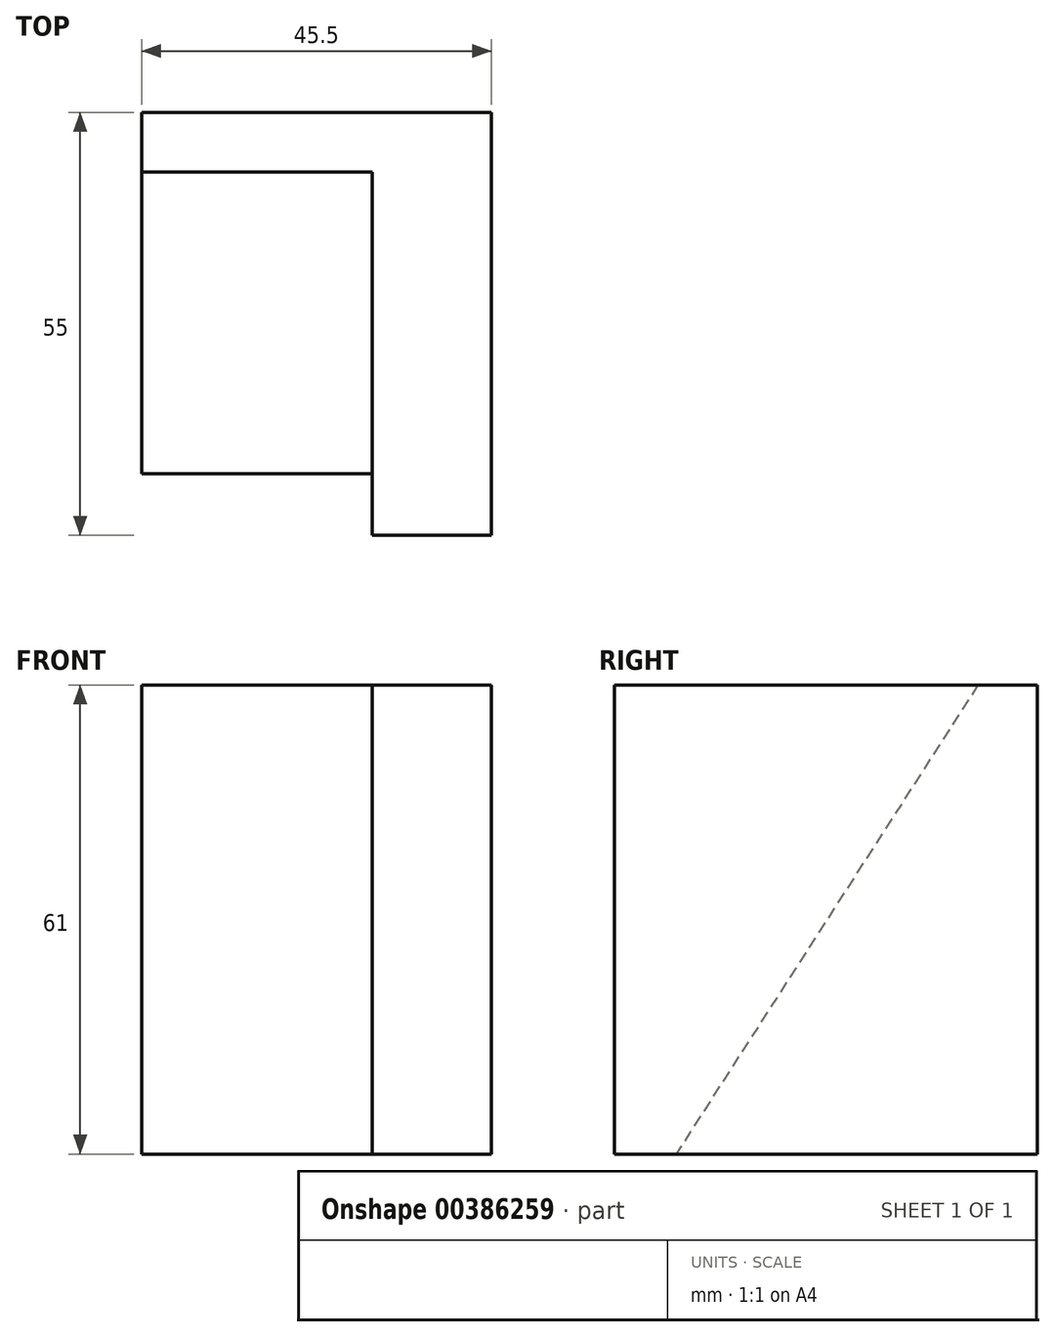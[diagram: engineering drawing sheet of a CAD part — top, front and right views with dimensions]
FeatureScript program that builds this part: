
annotation { "Feature Type Name" : "Feature", "Feature Type Description" : "" }
export const myFeature = defineFeature(function(context is Context, id is Id, definition is map)
    precondition{}
    {
        {
            var Q0;
            Q0=qCreatedBy(makeId("Front.planeOp"),FACE);
            var sketch = newSketch(context, id + "F0", { "sketchPlane" : qUnion([Q0])});
            skLineSegment(sketch, "E0", {"start": v(-30.5, 0) * mm, "end": v(-99.5, 0) * mm});
            skLineSegment(sketch, "E1", {"start": v(30.5, 0) * mm, "end": v(99.5, 0) * mm});
            skLineSegment(sketch, "E2", {"start": v(-99.5, 0) * mm, "end": v(-99.5, 15) * mm});
            skLineSegment(sketch, "E3", {"start": v(-99.5, 15) * mm, "end": v(-30.5, 15) * mm});
            skLineSegment(sketch, "E4", {"start": v(-30.5, 15) * mm, "end": v(-30.5, 0) * mm});
            skLineSegment(sketch, "E5", {"start": v(99.5, 0) * mm, "end": v(99.5, 15) * mm});
            skLineSegment(sketch, "E6", {"start": v(99.5, 15) * mm, "end": v(30.5, 15) * mm});
            skLineSegment(sketch, "E7", {"start": v(30.5, 15) * mm, "end": v(30.5, 0) * mm});
            skLineSegment(sketch, "E8", {"start": v(-30.5, 15) * mm, "end": v(-30.5, 61) * mm});
            skLineSegment(sketch, "E9", {"start": v(30.5, 61) * mm, "end": v(30.5, 15) * mm});
            skLineSegment(sketch, "E10", {"start": v(-30.5, 0) * mm, "end": v(-15, 0) * mm});
            skLineSegment(sketch, "E11", {"start": v(-15, 0) * mm, "end": v(15, 0) * mm});
            skLineSegment(sketch, "E12", {"start": v(15, 0) * mm, "end": v(30.5, 0) * mm});
            skLineSegment(sketch, "E13", {"start": v(-15, 0) * mm, "end": v(-15, 61) * mm});
            skLineSegment(sketch, "E14", {"start": v(30.5, 61) * mm, "end": v(-30.5, 61) * mm});
            skLineSegment(sketch, "E15", {"start": v(15, 0) * mm, "end": v(15, 61) * mm});
            skSolve(sketch);
        }
        {
            var Q0;
            Q0=makeQuery(id+"F0.imprint","IMPRINT",FACE,{"disambiguationData":[TD([[makeQuery(id+"F0.imprint","IMPRINT",EDGE,{"derivedFrom":sQuery(id+"F0.wireOp",EDGE,"E7")}),-1.0]])]});
            extrude(context, id + "F1", {"entities" : qUnion([Q0]), "depth" : 55 * mm});
        }
        {
            var Q0;
            Q0=makeQuery(id+"F1.opExtrude","SWEPT_FACE",FACE,{"disambiguationData":[OSD([sQuery(id+"F0.wireOp",EDGE,"E15")])]});
            var sketch = newSketch(context, id + "F2", { "sketchPlane" : qUnion([Q0])});
            skLineSegment(sketch, "E16", {"start": v(0, 61) * mm, "end": v(7.75, 61) * mm});
            skLineSegment(sketch, "E17", {"start": v(7.75, 61) * mm, "end": v(47, 0) * mm});
            skLineSegment(sketch, "E18", {"start": v(47, 0) * mm, "end": v(0, 0) * mm});
            skLineSegment(sketch, "E19", {"start": v(0, 0) * mm, "end": v(0, 61) * mm});
            skSolve(sketch);
        }
        {
            var Q0;
            Q0=makeQuery(id+"F2.imprint","IMPRINT",FACE,{"disambiguationData":[TD([[makeQuery(id+"F2.imprint","IMPRINT",EDGE,{"derivedFrom":sQuery(id+"F2.wireOp",EDGE,"E16")}),1.0]])]});
            extrude(context, id + "F3", {"entities" : qUnion([Q0]), "operationType" : NewBodyOperationType.ADD, "depth" : 30 * mm});
        }
    });
